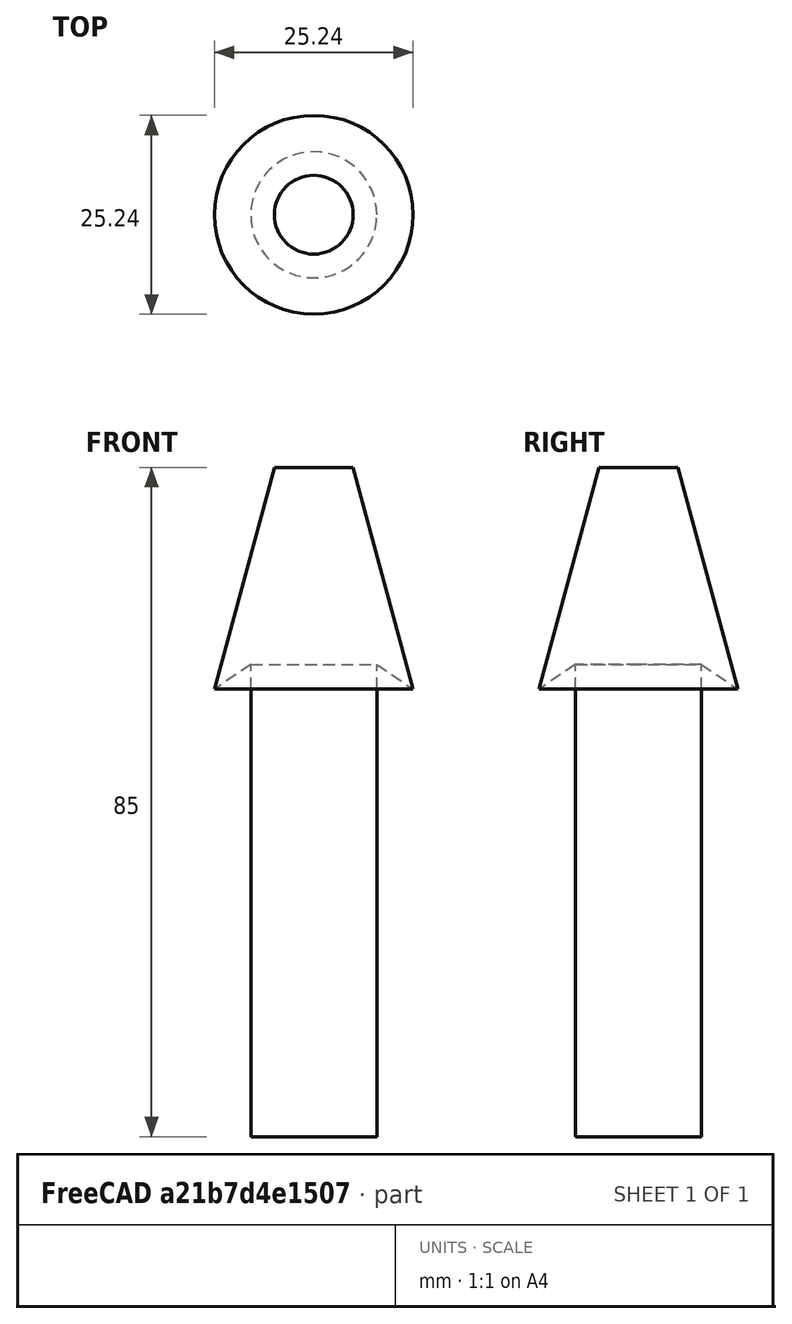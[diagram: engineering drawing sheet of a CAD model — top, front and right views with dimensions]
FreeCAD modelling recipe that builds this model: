
FCSTD DOCUMENT  (FreeCAD 0.19R24291 (Git))
Label: prograde marker
License: All rights reserved
LicenseURL: http://en.wikipedia.org/wiki/All_rights_reserved
objects: Sketcher::SketchObject×1, PartDesign::Revolution×1, PartDesign::Body×1
note: 4 computed .brp shape members not serialized (recipe doc carries the construction recipe); baked Part::Feature solids carry a one-line shape summary decoded from their .brp

FEATURE [Sketcher::SketchObject] Sketch
  FullyConstrained = false
  MapMode = 5
  Placement = pos=(0,0,0) rot=(1,0,0;1.5708rad)
  Support = -> [XZ_Plane]
  sketch-geometry (6):
    g0: LineSegment StartX=0 StartY=0 StartZ=0 EndX=-8 EndY=0 EndZ=0
    g1: LineSegment StartX=-8 StartY=0 StartZ=0 EndX=-8 EndY=60 EndZ=0
    g2: LineSegment StartX=-8 StartY=60 StartZ=0 EndX=-12.6177 EndY=56.841 EndZ=0
    g3: LineSegment StartX=0 StartY=85 StartZ=0 EndX=0 EndY=0 EndZ=0
    g4: LineSegment StartX=0 StartY=85 StartZ=0 EndX=-5 EndY=85 EndZ=0
    g5: LineSegment StartX=-5 StartY=85 StartZ=0 EndX=-12.6177 EndY=56.841 EndZ=0
  constraints (15):
    c: Coincident(g0,g1)
    c: Coincident(g1,g2)
    c: Vertical(g3)
    c: Coincident(g0,g3)
    c: Horizontal(g0)
    c: Vertical(g1)
    c: Coincident(g0,g-1)
    c: Coincident(g4,g3)
    c: Horizontal(g4)
    c: Coincident(g5,g4)
    c: Coincident(g5,g2)
    c: Distance(g0) = 8
    c: Distance(g3) = 85
    c: Distance(g1) = 60
    c: Distance(g4) = 5
FEATURE [PartDesign::Revolution] Revolution
  Angle = 360
  Axis = (0,2e-16,1)
  Base = (0,0,0)
  Placement = pos=(0,0,0) rot=(1,0,0;1.5708rad)
  Profile = -> Sketch
  ReferenceAxis = -> Sketch [V_Axis]
FEATURE [PartDesign::Body] Body
  Group = -> [Sketch,Revolution]
  Origin = -> Origin
  Tip = -> Revolution
